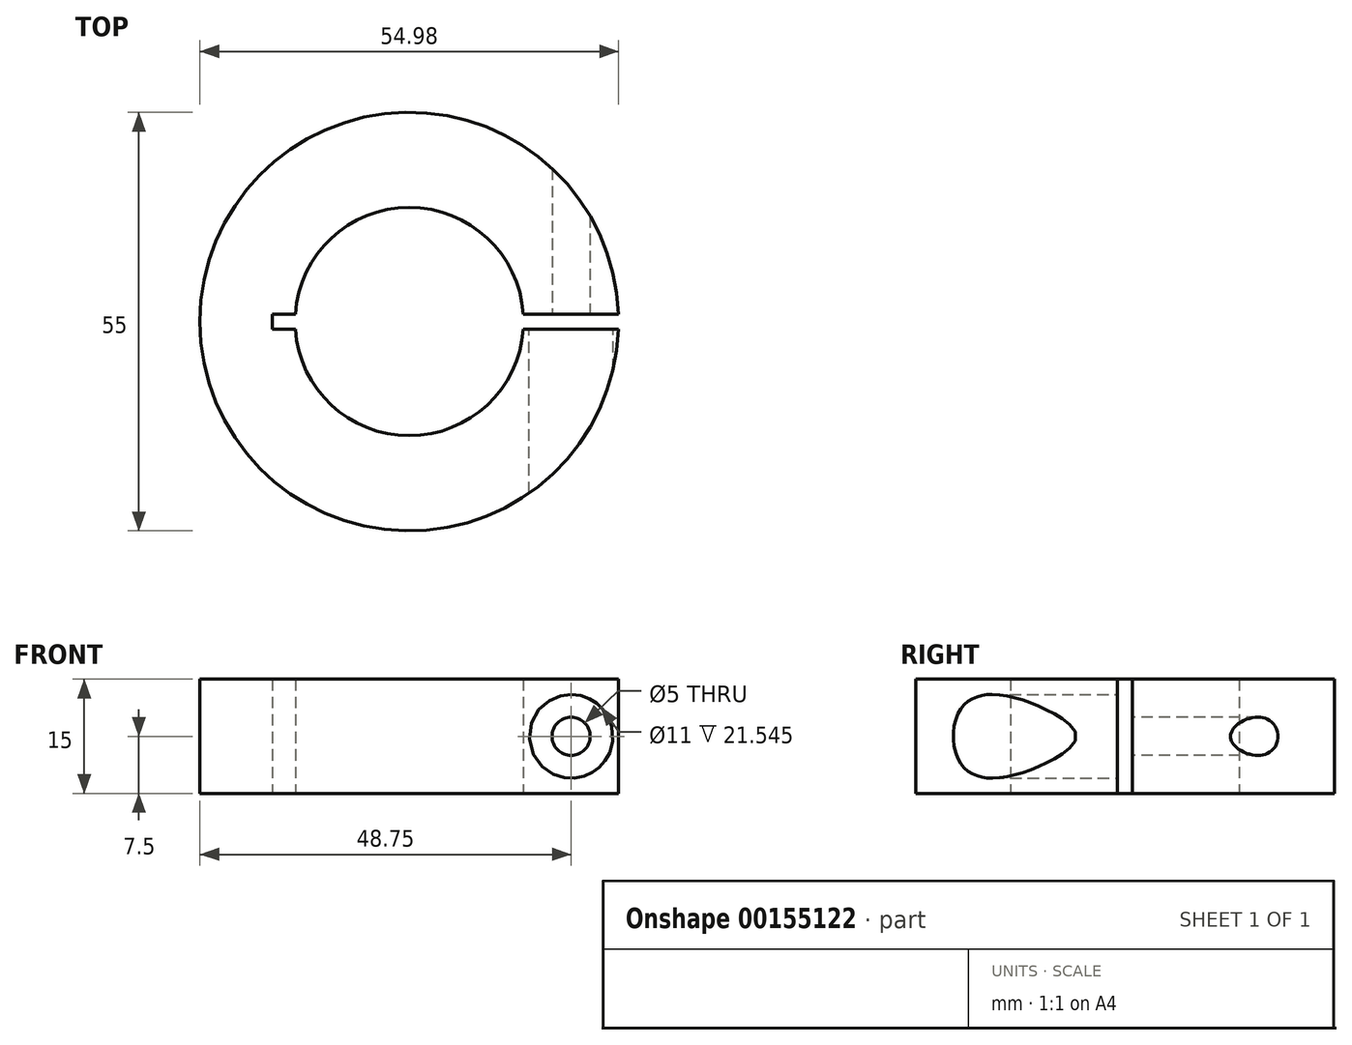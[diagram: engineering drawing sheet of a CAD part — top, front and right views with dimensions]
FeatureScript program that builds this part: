
annotation { "Feature Type Name" : "Feature", "Feature Type Description" : "" }
export const myFeature = defineFeature(function(context is Context, id is Id, definition is map)
    precondition{}
    {
        {
            var Q0;
            Q0=qCreatedBy(makeId("Top.planeOp"),FACE);
            var sketch = newSketch(context, id + "F0", { "sketchPlane" : qUnion([Q0])});
            skCircle(sketch, "E0", {"center": v(0, 0) * mm, "radius": 15 * mm});
            skCircle(sketch, "E1", {"center": v(0, 0) * mm, "radius": 27.5 * mm});
            skLineSegment(sketch, "E2.bottom", {"start": v(-17.97, 1) * mm, "end": v(28.48, 1) * mm});
            skLineSegment(sketch, "E2.top", {"start": v(-17.97, -1) * mm, "end": v(28.48, -1) * mm});
            skLineSegment(sketch, "E2.left", {"start": v(-17.97, 1) * mm, "end": v(-17.97, -1) * mm});
            skLineSegment(sketch, "E2.right", {"start": v(28.48, 1) * mm, "end": v(28.48, -1) * mm});
            skPoint(sketch, "E2.middle", {"position": v(5.26, 0) * mm});
            skSolve(sketch);
        }
        {
            var Q0;
            {var subQ0=sQuery(id+"F0.wireOp",EDGE,"E2.left");Q0=makeQuery(id+"F0.imprint","IMPRINT",FACE,{"disambiguationData":[TD([[makeQuery(id+"F0.imprint","IMPRINT",EDGE,{"derivedFrom":subQ0}),-1.0]])]});}
            extrude(context, id + "F1", {"entities" : qUnion([Q0]), "depth" : 15 * mm});
        }
        {
            var Q0;
            Q0=qCreatedBy(makeId("Front.planeOp"),FACE);
            var sketch = newSketch(context, id + "F2", { "sketchPlane" : qUnion([Q0])});
            skCircle(sketch, "E3", {"center": v(21.25, 7.5) * mm, "radius": 2.5 * mm});
            skCircle(sketch, "E4", {"center": v(21.25, 7.5) * mm, "radius": 5.5 * mm});
            skLineSegment(sketch, "E5", {"start": v(-27.5, 0) * mm, "end": v(-27.5, 15) * mm});
            skLineSegment(sketch, "E6.0", {"start": v(27.48, 15) * mm, "end": v(27.48, 0) * mm});
            skLineSegment(sketch, "E7", {"start": v(-27.5, 7.5) * mm, "end": v(21.25, 7.5) * mm, "construction": true});
            skLineSegment(sketch, "E8.0", {"start": v(27.48, 15) * mm, "end": v(-27.5, 15) * mm});
            skSolve(sketch);
        }
        {
            var Q0;
            Q0=makeQuery(id+"F2.imprint","IMPRINT",FACE,{"disambiguationData":[TD([[makeQuery(id+"F2.imprint","IMPRINT",EDGE,{"derivedFrom":sQuery(id+"F2.wireOp",EDGE,"E3")}),1.0]])]});
            extrude(context, id + "F3", {"entities" : qUnion([Q0]), "operationType" : NewBodyOperationType.REMOVE, "endBound" : BoundingType.THROUGH_ALL, "oppositeDirection" : true, "depth" : 25 * mm});
        }
        {
            var Q0;
            Q0=makeQuery(id+"F2.imprint","IMPRINT",FACE,{"disambiguationData":[TD([[makeQuery(id+"F2.imprint","IMPRINT",EDGE,{"derivedFrom":sQuery(id+"F2.wireOp",EDGE,"E3")}),-1.0]])]});
            var Q1;
            Q1=makeQuery(id+"F2.imprint","IMPRINT",FACE,{"disambiguationData":[TD([[makeQuery(id+"F2.imprint","IMPRINT",EDGE,{"derivedFrom":sQuery(id+"F2.wireOp",EDGE,"E3")}),1.0]])]});
            extrude(context, id + "F4", {"entities" : qUnion([Q0, Q1]), "operationType" : NewBodyOperationType.REMOVE, "endBound" : BoundingType.THROUGH_ALL, "depth" : 25 * mm});
        }
    });
